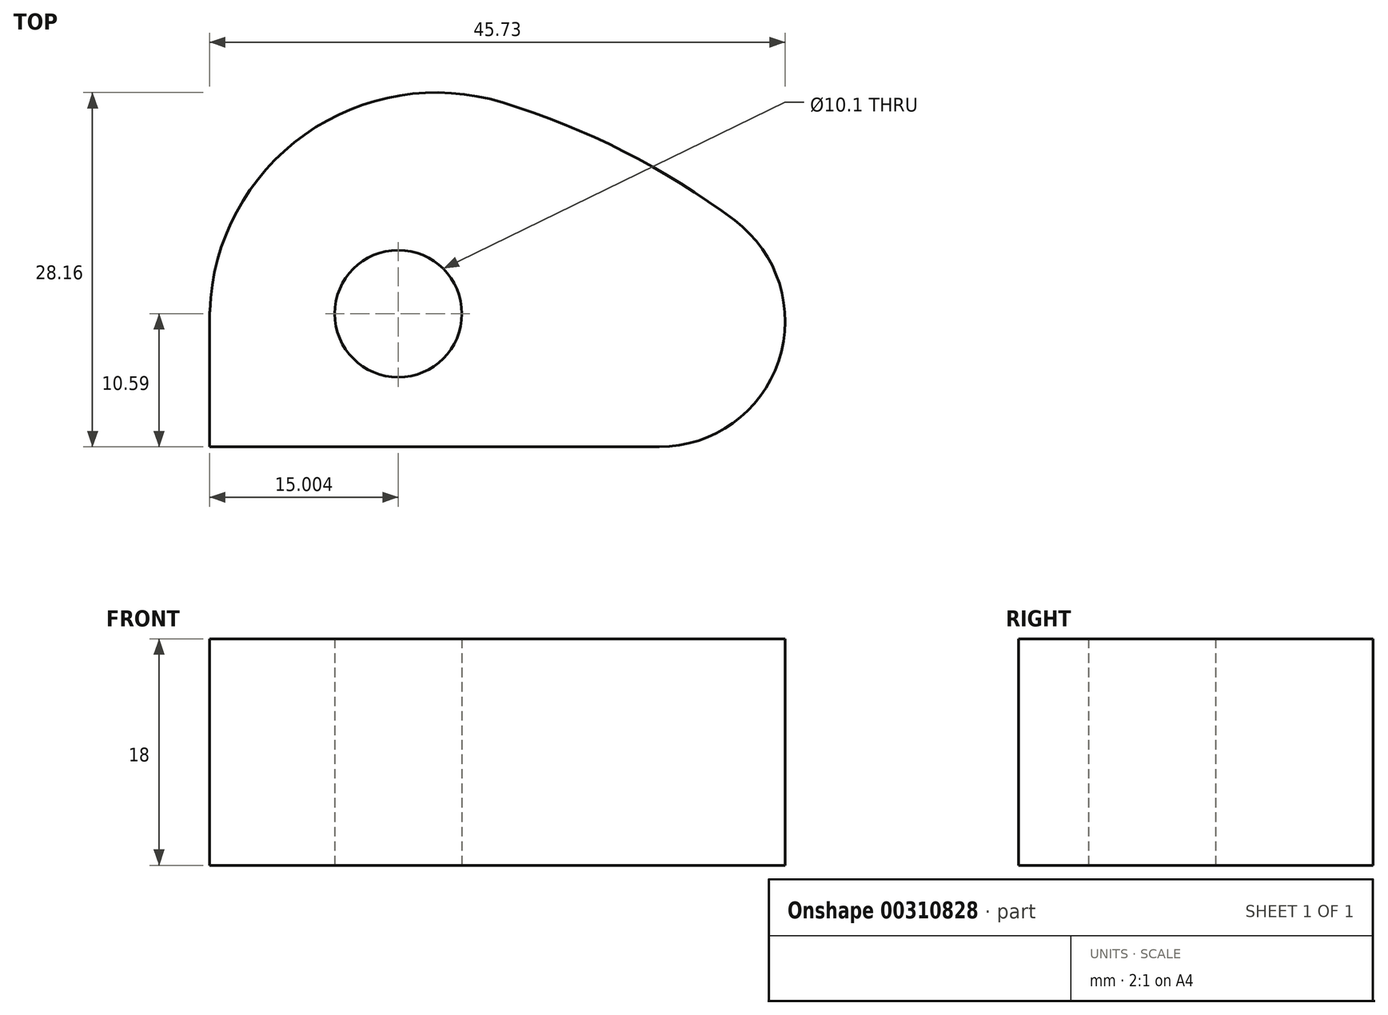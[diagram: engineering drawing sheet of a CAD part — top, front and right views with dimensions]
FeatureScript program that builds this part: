
annotation { "Feature Type Name" : "Feature", "Feature Type Description" : "" }
export const myFeature = defineFeature(function(context is Context, id is Id, definition is map)
    precondition{}
    {
        {
            var Q0;
            Q0=qCreatedBy(makeId("Top.planeOp"),FACE);
            var sketch = newSketch(context, id + "F0", { "sketchPlane" : qUnion([Q0])});
            skLineSegment(sketch, "E0", {"start": v(-17.33, 0) * mm, "end": v(42.67, 0) * mm});
            skLineSegment(sketch, "E1", {"start": v(42.67, 0) * mm, "end": v(12.67, 30) * mm});
            skLineSegment(sketch, "E2", {"start": v(12.67, 30) * mm, "end": v(-17.33, 30) * mm});
            skLineSegment(sketch, "E3", {"start": v(-17.33, 30) * mm, "end": v(-17.33, 0) * mm});
            skLineSegment(sketch, "E4", {"start": v(-17.33, 10.6) * mm, "end": v(32.08, 10.59) * mm, "construction": true});
            skCircle(sketch, "E5", {"center": v(-2.33, 10.6) * mm, "radius": 5.05 * mm});
            skLineSegment(sketch, "E6", {"start": v(-2.33, 30) * mm, "end": v(-2.33, 0) * mm, "construction": true});
            skSolve(sketch);
        }
        {
            var Q0;
            Q0 = qSketchRegion(id + "F0", true);
            extrude(context, id + "F1", {"entities" : qUnion([Q0]), "depth" : 18 * mm});
        }
        {
            var Q0;
            Q0=makeQuery(id+"F1.opExtrude","SWEPT_EDGE",EDGE,{"disambiguationData":[OSD([sQuery(id+"F0.wireOp",EDGE,"E0"),sQuery(id+"F0.wireOp",EDGE,"E1")])]});
            fillet(context, id + "F2", {"entities" : qUnion([Q0]), "radius" : 10 * mm, "tangentPropagation" : true, "allowEdgeOverflow" : false});
        }
        {
            var Q0;
            Q0=makeQuery(id+"F1.opExtrude","SWEPT_EDGE",EDGE,{"disambiguationData":[OSD([sQuery(id+"F0.wireOp",EDGE,"E1"),sQuery(id+"F0.wireOp",EDGE,"E2")])]});
            fillet(context, id + "F3", {"entities" : qUnion([Q0]), "radius" : 60 * mm, "tangentPropagation" : true, "allowEdgeOverflow" : false});
        }
        {
            var Q0;
            {var subQ0=sQuery(id+"F0.wireOp",EDGE,"E1");Q0=makeQuery(id+"F3.opFillet","BLEND_EDGE",EDGE,{"blendedFrom":[makeQuery(id+"F1.opExtrude","SWEPT_EDGE",EDGE,{"disambiguationData":[OSD([subQ0,sQuery(id+"F0.wireOp",EDGE,"E2")])]}),makeQuery(id+"F2.opFillet","BLEND_FACE",FACE,{"disambiguationData":[OSD([sQuery(id+"F0.wireOp",EDGE,"E0"),subQ0])]})],"blendedInto":[makeQuery(id+"F2.opFillet","BLEND_FACE",FACE,{"disambiguationData":[OSD([sQuery(id+"F0.wireOp",EDGE,"E0"),subQ0])]})]});}
            fillet(context, id + "F4", {"entities" : qUnion([Q0]), "radius" : 10 * mm, "tangentPropagation" : true, "allowEdgeOverflow" : false});
        }
        {
            var Q0;
            Q0=makeQuery(id+"F1.opExtrude","SWEPT_EDGE",EDGE,{"disambiguationData":[OSD([sQuery(id+"F0.wireOp",EDGE,"E2"),sQuery(id+"F0.wireOp",EDGE,"E3")])]});
            fillet(context, id + "F5", {"entities" : qUnion([Q0]), "radius" : 40 * mm, "tangentPropagation" : true, "allowEdgeOverflow" : false});
        }
        {
            var Q0;
            {var subQ0=sQuery(id+"F0.wireOp",EDGE,"E2");Q0=makeQuery(id+"F5.opFillet","BLEND_EDGE",EDGE,{"blendedFrom":[makeQuery(id+"F1.opExtrude","SWEPT_EDGE",EDGE,{"disambiguationData":[OSD([subQ0,sQuery(id+"F0.wireOp",EDGE,"E3")])]}),makeQuery(id+"F3.opFillet","BLEND_FACE",FACE,{"disambiguationData":[OSD([sQuery(id+"F0.wireOp",EDGE,"E1"),subQ0])]})],"blendedInto":[makeQuery(id+"F3.opFillet","BLEND_FACE",FACE,{"disambiguationData":[OSD([sQuery(id+"F0.wireOp",EDGE,"E1"),subQ0])]})]});}
            fillet(context, id + "F6", {"entities" : qUnion([Q0]), "radius" : 18 * mm, "tangentPropagation" : true, "allowEdgeOverflow" : false});
        }
    });
